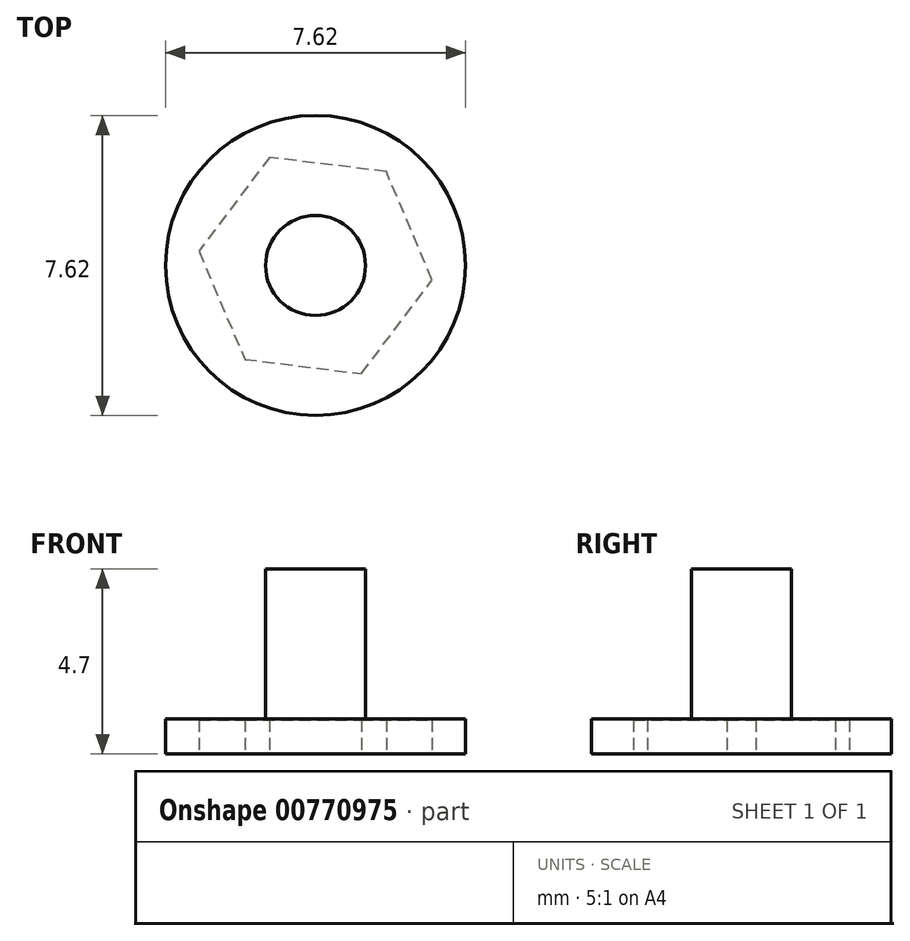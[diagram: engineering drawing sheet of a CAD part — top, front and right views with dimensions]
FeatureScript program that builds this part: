
annotation { "Feature Type Name" : "Feature", "Feature Type Description" : "" }
export const myFeature = defineFeature(function(context is Context, id is Id, definition is map)
    precondition{}
    {
        {
            var Q0;
            Q0=qCreatedBy(makeId("Top.planeOp"),FACE);
            var sketch = newSketch(context, id + "F0", { "sketchPlane" : qUnion([Q0])});
            skCircle(sketch, "E0", {"center": v(0, 0) * mm, "radius": 3.81 * mm});
            skSolve(sketch);
        }
        {
            var Q0;
            Q0=makeQuery(id+"F0.imprint","IMPRINT",FACE,{"disambiguationData":[TD([[makeQuery(id+"F0.imprint","IMPRINT",EDGE,{"derivedFrom":sQuery(id+"F0.wireOp",EDGE,"E0")}),1.0]])]});
            extrude(context, id + "F1", {"entities" : qUnion([Q0]), "depth" : 0.89 * mm, "offsetDistance" : 25.4 * mm});
        }
        {
            var Q0;
            Q0=makeQuery(id+"F1.opExtrude","CAP_FACE",FACE,{"disambiguationData":[OSD([sQuery(id+"F0.wireOp",EDGE,"E0")])],"isStart":false});
            var sketch = newSketch(context, id + "F2", { "sketchPlane" : qUnion([Q0])});
            skCircle(sketch, "E1", {"center": v(0, 0) * mm, "radius": 1.27 * mm});
            skSolve(sketch);
        }
        {
            var Q0;
            Q0=makeQuery(id+"F2.imprint","IMPRINT",FACE,{"disambiguationData":[TD([[makeQuery(id+"F2.imprint","IMPRINT",EDGE,{"derivedFrom":sQuery(id+"F2.wireOp",EDGE,"E1")}),1.0]])]});
            extrude(context, id + "F3", {"entities" : qUnion([Q0]), "operationType" : NewBodyOperationType.ADD, "depth" : 3.8 * mm, "offsetDistance" : 25.4 * mm});
        }
        {
            var Q0;
            Q0=makeQuery(id+"F1.opExtrude","CAP_FACE",FACE,{"disambiguationData":[OSD([sQuery(id+"F0.wireOp",EDGE,"E0")])],"isStart":true});
            var sketch = newSketch(context, id + "F4", { "sketchPlane" : qUnion([Q0])});
            skCircle(sketch, "E2.cCircle", {"center": v(0, 0) * mm, "radius": 2.59 * mm, "construction": true});
            skLineSegment(sketch, "E2.0", {"start": v(1.17, 2.75) * mm, "end": v(2.96, 0.36) * mm});
            skLineSegment(sketch, "E2.1", {"start": v(2.96, 0.36) * mm, "end": v(1.8, -2.38) * mm});
            skLineSegment(sketch, "E2.2", {"start": v(1.8, -2.38) * mm, "end": v(-1.17, -2.75) * mm});
            skLineSegment(sketch, "E2.3", {"start": v(-1.17, -2.75) * mm, "end": v(-2.96, -0.36) * mm});
            skLineSegment(sketch, "E2.4", {"start": v(-2.96, -0.36) * mm, "end": v(-1.8, 2.38) * mm});
            skLineSegment(sketch, "E2.5", {"start": v(-1.8, 2.38) * mm, "end": v(1.17, 2.75) * mm});
            skPoint(sketch, "E2.0.midPoint", {"position": v(2.06, 1.56) * mm});
            skSolve(sketch);
        }
        {
            var Q0;
            Q0=makeQuery(id+"F4.imprint","IMPRINT",FACE,{"disambiguationData":[TD([[makeQuery(id+"F4.imprint","IMPRINT",EDGE,{"derivedFrom":sQuery(id+"F4.wireOp",EDGE,"E2.0")}),-1.0]])]});
            extrude(context, id + "F5", {"entities" : qUnion([Q0]), "operationType" : NewBodyOperationType.REMOVE, "oppositeDirection" : true, "depth" : 0.86 * mm, "offsetDistance" : 25.4 * mm});
        }
    });
